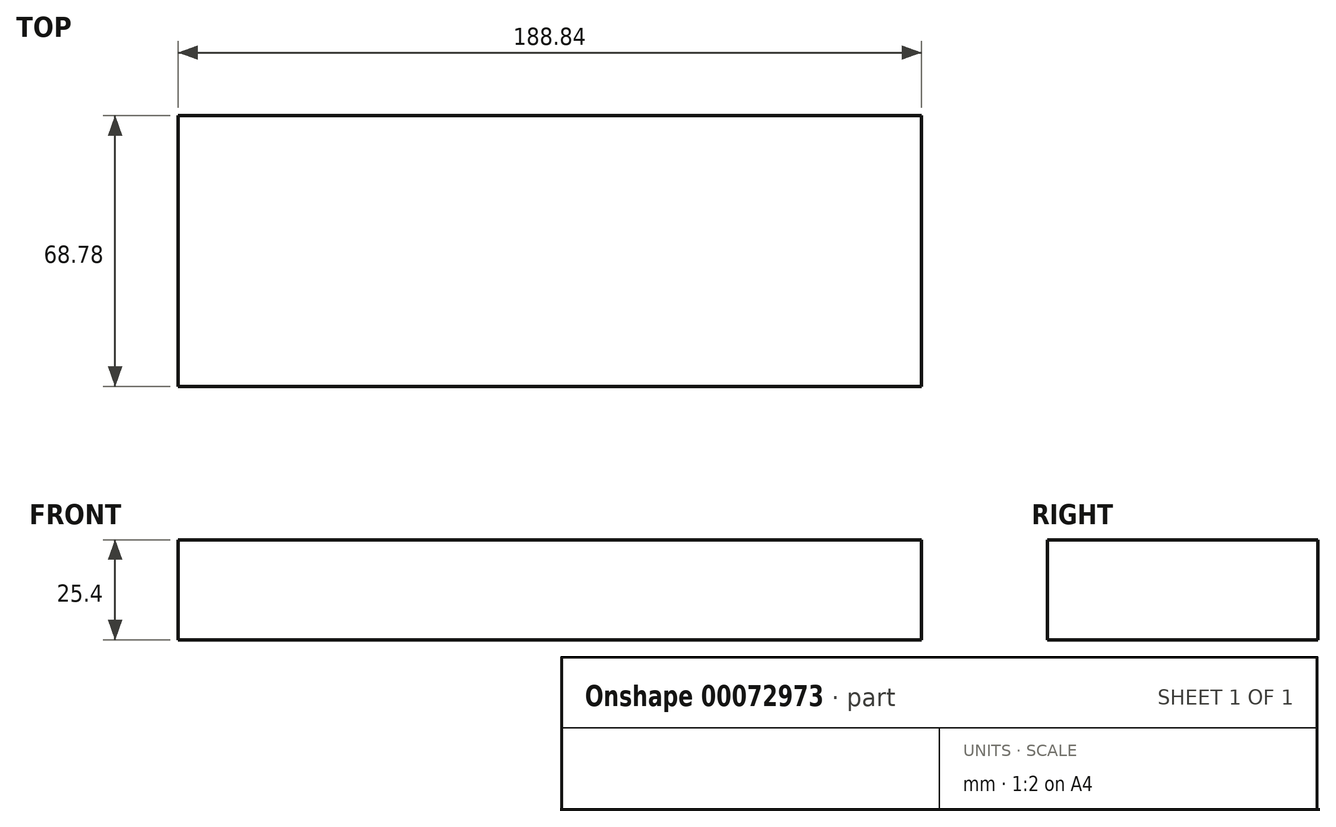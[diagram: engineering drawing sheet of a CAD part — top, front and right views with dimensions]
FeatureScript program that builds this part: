
annotation { "Feature Type Name" : "Feature", "Feature Type Description" : "" }
export const myFeature = defineFeature(function(context is Context, id is Id, definition is map)
    precondition{}
    {
        {
            var Q0;
            Q0=qCreatedBy(makeId("Top.planeOp"),FACE);
            var sketch = newSketch(context, id + "F0", { "sketchPlane" : qUnion([Q0])});
            skLineSegment(sketch, "E0.rect.bottom", {"start": v(-94.42, -34.4) * mm, "end": v(94.42, -34.4) * mm});
            skLineSegment(sketch, "E0.rect.top", {"start": v(-94.42, 34.4) * mm, "end": v(94.42, 34.4) * mm});
            skLineSegment(sketch, "E0.rect.left", {"start": v(-94.42, -34.4) * mm, "end": v(-94.42, 34.4) * mm});
            skLineSegment(sketch, "E0.rect.right", {"start": v(94.42, -34.4) * mm, "end": v(94.42, 34.4) * mm});
            skPoint(sketch, "E0.rect.middle", {"position": v(0, 0) * mm});
            skSolve(sketch);
        }
        {
            var Q0;
            Q0=makeQuery(id+"F0.imprint","IMPRINT",FACE,{"disambiguationData":[TD([[makeQuery(id+"F0.imprint","IMPRINT",EDGE,{"derivedFrom":sQuery(id+"F0.wireOp",EDGE,"E0.rect.bottom")}),1.0]])]});
            extrude(context, id + "F1", {"entities" : qUnion([Q0]), "depth" : 25.4 * mm});
        }
    });
